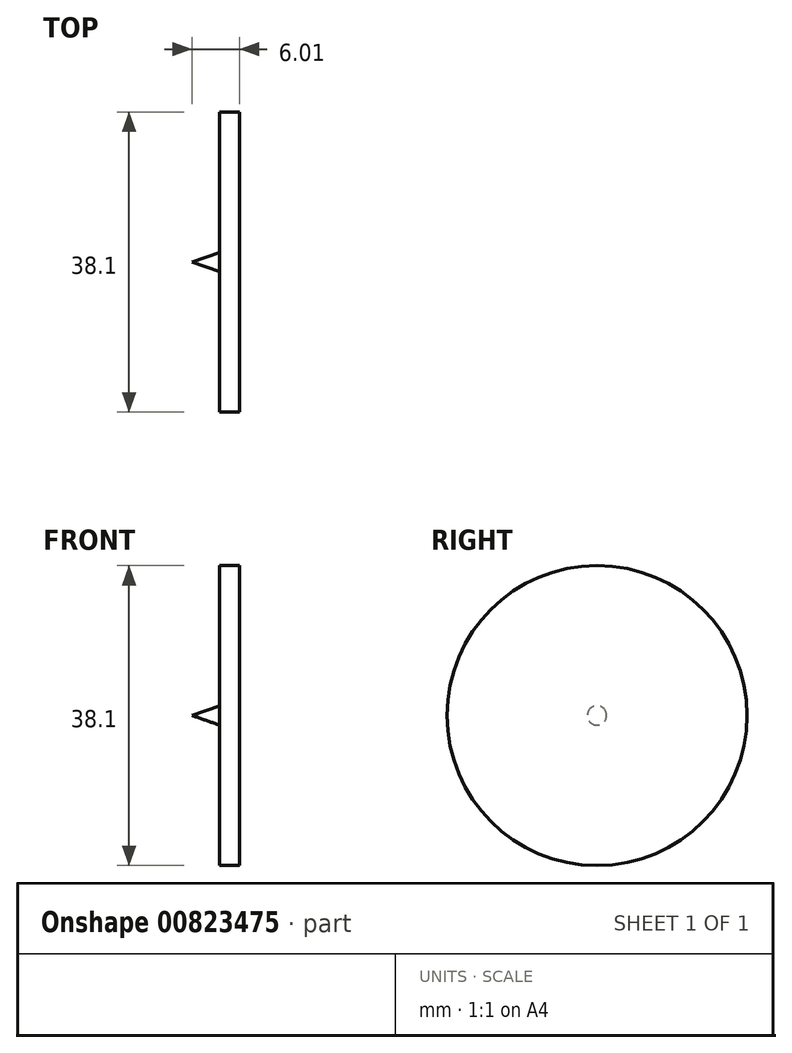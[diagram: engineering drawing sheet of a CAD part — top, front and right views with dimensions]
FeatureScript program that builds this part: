
annotation { "Feature Type Name" : "Feature", "Feature Type Description" : "" }
export const myFeature = defineFeature(function(context is Context, id is Id, definition is map)
    precondition{}
    {
        {
            var Q0;
            Q0=qCreatedBy(makeId("Front.planeOp"),FACE);
            var sketch = newSketch(context, id + "F0", { "sketchPlane" : qUnion([Q0])});
            skLineSegment(sketch, "E0", {"start": v(0, 19.05) * mm, "end": v(2.5, 19.05) * mm});
            skLineSegment(sketch, "E1", {"start": v(2.5, 19.05) * mm, "end": v(2.5, 0) * mm});
            skLineSegment(sketch, "E2", {"start": v(2.5, 0) * mm, "end": v(0, 0) * mm});
            skLineSegment(sketch, "E3.0.5.0", {"start": v(0, 0) * mm, "end": v(-3.5, 0) * mm});
            skLineSegment(sketch, "E3.0.5.1", {"start": v(-3.5, 0) * mm, "end": v(0, 1.23) * mm});
            skLineSegment(sketch, "E4", {"start": v(0, 19.05) * mm, "end": v(0, 18.38) * mm});
            skLineSegment(sketch, "E5", {"start": v(0, 1.23) * mm, "end": v(-3.38, 1.23) * mm});
            skLineSegment(sketch, "E6", {"start": v(0, 1.23) * mm, "end": v(0, 2.96) * mm});
            skLineSegment(sketch, "E7", {"start": v(0, 2.96) * mm, "end": v(-3.25, 2.96) * mm});
            skLineSegment(sketch, "E8", {"start": v(0, 2.96) * mm, "end": v(0, 5.1) * mm});
            skLineSegment(sketch, "E9", {"start": v(0, 5.1) * mm, "end": v(0, 7.56) * mm});
            skLineSegment(sketch, "E10", {"start": v(0, 7.56) * mm, "end": v(0, 10.32) * mm});
            skLineSegment(sketch, "E11", {"start": v(0, 10.32) * mm, "end": v(0, 13.34) * mm});
            skLineSegment(sketch, "E12", {"start": v(0, 13.34) * mm, "end": v(0, 16.62) * mm});
            skLineSegment(sketch, "E13", {"start": v(0, 16.62) * mm, "end": v(0, 20.13) * mm});
            skLineSegment(sketch, "E14", {"start": v(0, 20.13) * mm, "end": v(0.76, 15.67) * mm});
            skSolve(sketch);
        }
        {
            var Q0;
            Q0=makeQuery(id+"F0.imprint","IMPRINT",FACE,{"disambiguationData":[TD([[makeQuery(id+"F0.imprint","IMPRINT",EDGE,{"derivedFrom":sQuery(id+"F0.wireOp",EDGE,"E0")}),-1.0]])]});
            var Q1;
            Q1=sQuery(id+"F0.wireOp",EDGE,"E2");
            revolve(context, id + "F1", {"surfaceOperationType" : NewSurfaceOperationType.NEW, "entities" : qUnion([Q0]), "axis" : qUnion([Q1]), "revolveType" : RevolveType.FULL});
        }
    });
